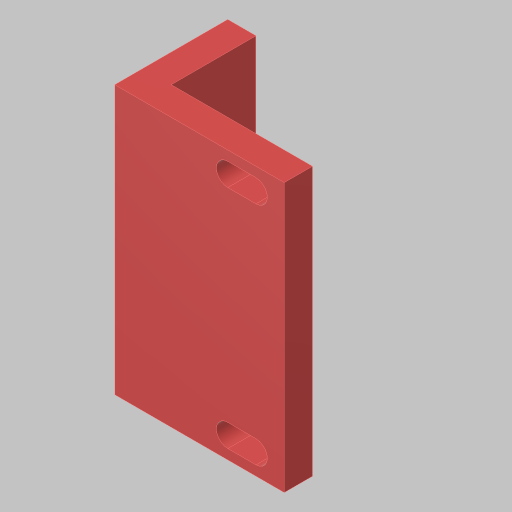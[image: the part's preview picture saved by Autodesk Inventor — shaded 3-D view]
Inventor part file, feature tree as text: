
AUTODESK INVENTOR PART (.ipt)
format: ipt  version: 2023.5 (Build 275446000, 446)  size: 135,168 bytes
history: native  units: in
note: dims shown in document units (in); Inventor stores cm internally (conversion verified against a paired STEP export)
features: sketch x3, extrude x2, hole x1
ambient origin geometry x8: Origin, YZ Plane, XZ Plane, XY Plane, X Axis, Y Axis, Z Axis, Center Point
bodies: Solid1 (feature_tree)
feature tree (6):
  extrude  "Extrusion1"  Depth=1.5in
  sketch  "Sketch2"  dims[d2=1.0in d3=2.375in d4=0.0in]
  hole  "Hole2"  [1 undecoded]
  extrude  "Extrusion2"  Depth=0.25in
  sketch  "Sketch1"  dims[d0=0.25in d1=1.5in]
  sketch  "Sketch3"  dims[d5=2.0in d6=0.25in d14=1.2598in d15=0.104in d16=0.276in d17=0.279in d18=0.25in d19=0.5635in d20=0.75in d21=0.8108in d23=0.325in d24=0.201in d25=0.25in d26=1.0in d27=0.0in]
note: 1 required parameter value undecoded (feature->parameter linkage not recoverable at this tier; creation-order binding heuristic only, values carry confidence <= 0.55)
